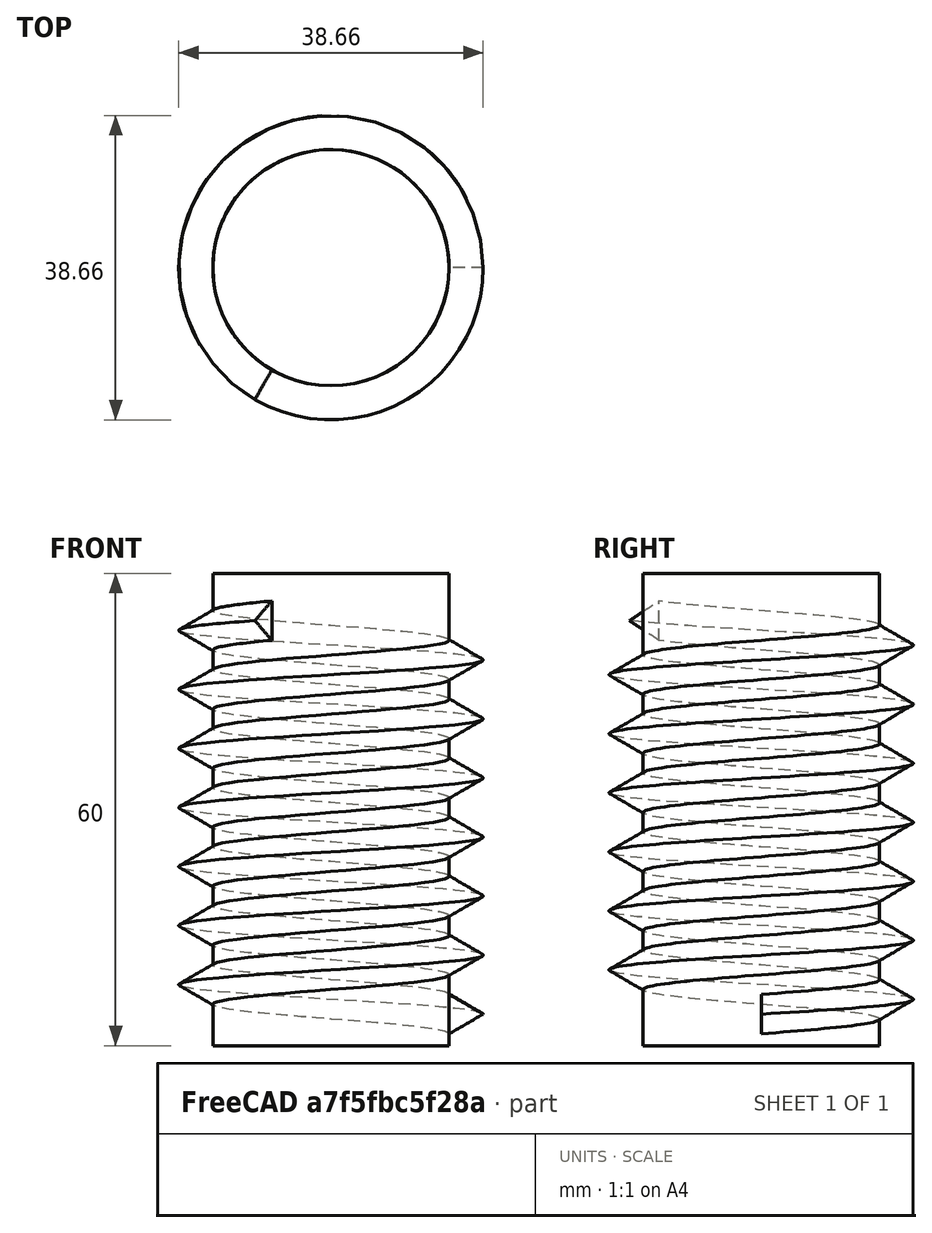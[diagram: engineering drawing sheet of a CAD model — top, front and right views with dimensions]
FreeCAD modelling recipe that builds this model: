
FCSTD DOCUMENT  (FreeCAD 0.17R13541 (Git))
Label: 阿基米德螺旋 带图纸
License: All rights reserved
LicenseURL: http://en.wikipedia.org/wiki/All_rights_reserved
objects: TechDraw::DrawViewDimension×5, TechDraw::DrawProjGroupItem×3, Part::Helix×1, PartDesign::FeatureBase×1, Sketcher::SketchObject×1, PartDesign::AdditivePipe×1, PartDesign::Body×1, Spreadsheet::Sheet×1, Part::Cylinder×1, Part::Fuse×1, TechDraw::DrawSVGTemplate×1, TechDraw::DrawProjGroup×1, TechDraw::DrawViewDetail×1, TechDraw::DrawPage×1
note: 8 computed .brp shape members not serialized (recipe doc carries the construction recipe); baked Part::Feature solids carry a one-line shape summary decoded from their .brp

FEATURE [Part::Helix] Helix  label="螺旋体"
  Angle = 0
  AttacherType = Attacher::AttachEngine3D
  Height = 50
  LocalCoord = 0
  Pitch = 7.5
  Radius = 15
  Style = 1
FEATURE [PartDesign::FeatureBase] BaseFeature
  BaseFeature = -> Helix
FEATURE [Sketcher::SketchObject] Sketch
  ExternalGeometry = -> [BaseFeature]
  MapMode = 5
  Placement = pos=(0,0,0) rot=(1,0,0;1.5708rad)
  Support = -> [XZ_Plane]
  sketch-geometry (4):
    g0: LineSegment StartX=19.3301 StartY=0 StartZ=0 EndX=12.8349 EndY=3.75 EndZ=0
    g1: LineSegment StartX=12.8349 StartY=3.75 StartZ=0 EndX=12.8349 EndY=-3.75 EndZ=0
    g2: LineSegment StartX=12.8349 StartY=-3.75 StartZ=0 EndX=19.3301 EndY=0 EndZ=0
    g3: Circle [constr] CenterX=15 CenterY=0 CenterZ=0 NormalX=0 NormalY=0 NormalZ=1 AngleXU=0 Radius=4.33013
  constraints (11):
    c: Coincident(g0,g1)
    c: Coincident(g1,g2)
    c: Coincident(g2,g0)
    c: Equal(g0,g1)
    c: Equal(g0,g2)
    c: PointOnObject(g0,g3)
    c: PointOnObject(g1,g3)
    c: PointOnObject(g2,g3)
    c: Coincident(g3,g-3)
    c: Vertical(g1)  '摆正三角形'
    c: DistanceY(g1,g0) = 7.5  '单边长度'
FEATURE [PartDesign::AdditivePipe] AdditivePipe
  AuxilleryCurvelinear = true
  AuxillerySpineTangent = false
  BaseFeature = -> BaseFeature
  Binormal = (0,0,0)
  Mode = 2
  Profile = -> Sketch
  Spine = -> BaseFeature [Edge1,Edge2,Edge3,Edge4,Edge5,Edge6,Edge7]
  SpineTangent = false
  Transformation = 0
  Transition = 0
FEATURE [PartDesign::Body] Body
  BaseFeature = -> Helix
  Group = -> [BaseFeature,Sketch,AdditivePipe]
  Origin = -> Origin
  Tip = -> AdditivePipe
FEATURE [Spreadsheet::Sheet] Spreadsheet
  cells = A2=Pitch; B2(pitch)=7.5; A3=Height; B3=50; A4=Radius; B4=15
FEATURE [Part::Cylinder] Cylinder  label="圆柱体"
  Angle = 360
  AttacherType = Attacher::AttachEngine3D
  Height = 60
  Placement = pos=(0,0,-4) rot=(0,0,1;0rad)
  Radius = 15
FEATURE [Part::Fuse] Fusion
  Base = -> Body
  Tool = -> Cylinder
FEATURE [TechDraw::DrawSVGTemplate] Template
  EditableTexts = AUTHOR_NAME=John Qu; DN=A1000-001; DRAWING_TITLE=阿基米德螺旋; FC-DATE=04/12/2018; FC-REV=REV A; FC-SC=1:1; FC-SH=1 / 1; FC-SI=A4; FreeCAD_DRAWING=FreeCAD DRAWING; PN=阿基米德螺旋
  Height = 297
  Orientation = 0
  Width = 210
FEATURE [TechDraw::DrawProjGroupItem] ProjItem  label="Front"
  CoarseView = false
  Direction = (0,-1,0)
  Focus = 100
  HardHidden = true
  IsoCount = 0
  IsoHidden = false
  IsoVisible = true
  LockPosition = true
  Perspective = false
  Rotation = 0
  RotationVector = (1,0,0)
  ScaleType = 0
  SeamHidden = false
  SeamVisible = true
  SmoothHidden = false
  SmoothVisible = false
  Source = -> [Fusion]
  Type = 0
  X = 0.0649667
  Y = -32.2643
FEATURE [TechDraw::DrawProjGroupItem] ProjItem001  label="Top"
  CoarseView = false
  Direction = (0,0,1)
  Focus = 100
  HardHidden = false
  IsoCount = 0
  IsoHidden = false
  IsoVisible = false
  LockPosition = false
  Perspective = false
  Rotation = 0
  RotationVector = (1,0,0)
  ScaleType = 0
  SeamHidden = false
  SeamVisible = false
  SmoothHidden = false
  SmoothVisible = false
  Source = -> [Fusion]
  Type = 4
  X = 0
  Y = 75
FEATURE [TechDraw::DrawProjGroupItem] ProjItem002  label="FrontTopRight"
  CoarseView = false
  Direction = (1,-1,1)
  Focus = 100
  HardHidden = false
  IsoCount = 0
  IsoHidden = false
  IsoVisible = false
  LockPosition = false
  Perspective = false
  Rotation = 0
  RotationVector = (1,-1,0)
  ScaleType = 0
  SeamHidden = false
  SeamVisible = false
  SmoothHidden = false
  SmoothVisible = false
  Source = -> [Fusion]
  Type = 7
  X = 81.3103
  Y = 81.3103
FEATURE [TechDraw::DrawProjGroup] ProjGroup
  Anchor = -> ProjItem
  AutoDistribute = true
  CubeDirs = (1) [(0,0,0)]
  CubeRotations = (1) [(0,0,0)]
  LockPosition = false
  ProjectionType = 0
  Rotation = 0
  ScaleType = 0
  Source = -> [Fusion]
  Views = -> [ProjItem,ProjItem001,ProjItem002]
  X = 67.7503
  Y = 147.502
  spacingX = 15
  spacingY = 15
FEATURE [TechDraw::DrawViewDimension] Dimension
  FormatSpec = %.2f
  LockPosition = false
  MeasureType = 1
  References2D = -> [ProjItem]
  Rotation = 0
  ScaleType = 0
  Type = 2
  X = -37.9149
  Y = 2.66069
FEATURE [TechDraw::DrawViewDetail] Detail
  AnchorPoint = (18,-25,0)
  BaseView = -> ProjItem
  CoarseView = false
  Direction = (0,-1,0)
  Focus = 100
  HardHidden = false
  IsoCount = 0
  IsoHidden = false
  IsoVisible = false
  LockPosition = false
  Perspective = false
  Radius = 10
  Reference = 1
  Rotation = 0
  Scale = 2
  ScaleType = 0
  SeamHidden = false
  SeamVisible = false
  SmoothHidden = false
  SmoothVisible = false
  Source = -> [Fusion]
  X = 152.56
  Y = 144.509
FEATURE [TechDraw::DrawViewDimension] Dimension001
  FormatSpec = %.2f
  LockPosition = false
  MeasureType = 1
  References2D = -> [Detail]
  Rotation = 0
  ScaleType = 0
  Type = 2
  X = 32.5935
  Y = 21.2856
FEATURE [TechDraw::DrawViewDimension] Dimension002
  FormatSpec = %.2f
  LockPosition = false
  MeasureType = 1
  References2D = -> [Detail]
  Rotation = 0
  ScaleType = 0
  Type = 2
  X = 24.2788
  Y = 21.6181
FEATURE [TechDraw::DrawViewDimension] Dimension003
  FormatSpec = ∅%.2f
  LockPosition = false
  MeasureType = 1
  References2D = -> [ProjItem]
  Rotation = 0
  ScaleType = 0
  Type = 1
  X = 0
  Y = 43.9
FEATURE [TechDraw::DrawViewDimension] Dimension005
  FormatSpec = %.2f
  LockPosition = false
  MeasureType = 1
  References2D = -> [Detail]
  Rotation = 0
  ScaleType = 0
  Type = 6
  X = -34.5689
  Y = -3.16351
FEATURE [TechDraw::DrawPage] Page
  KeepUpdated = true
  ProjectionType = 1
  Template = -> Template
  Views = -> [ProjGroup,Dimension,Detail,Dimension001,Dimension002,Dimension003,Dimension005]
